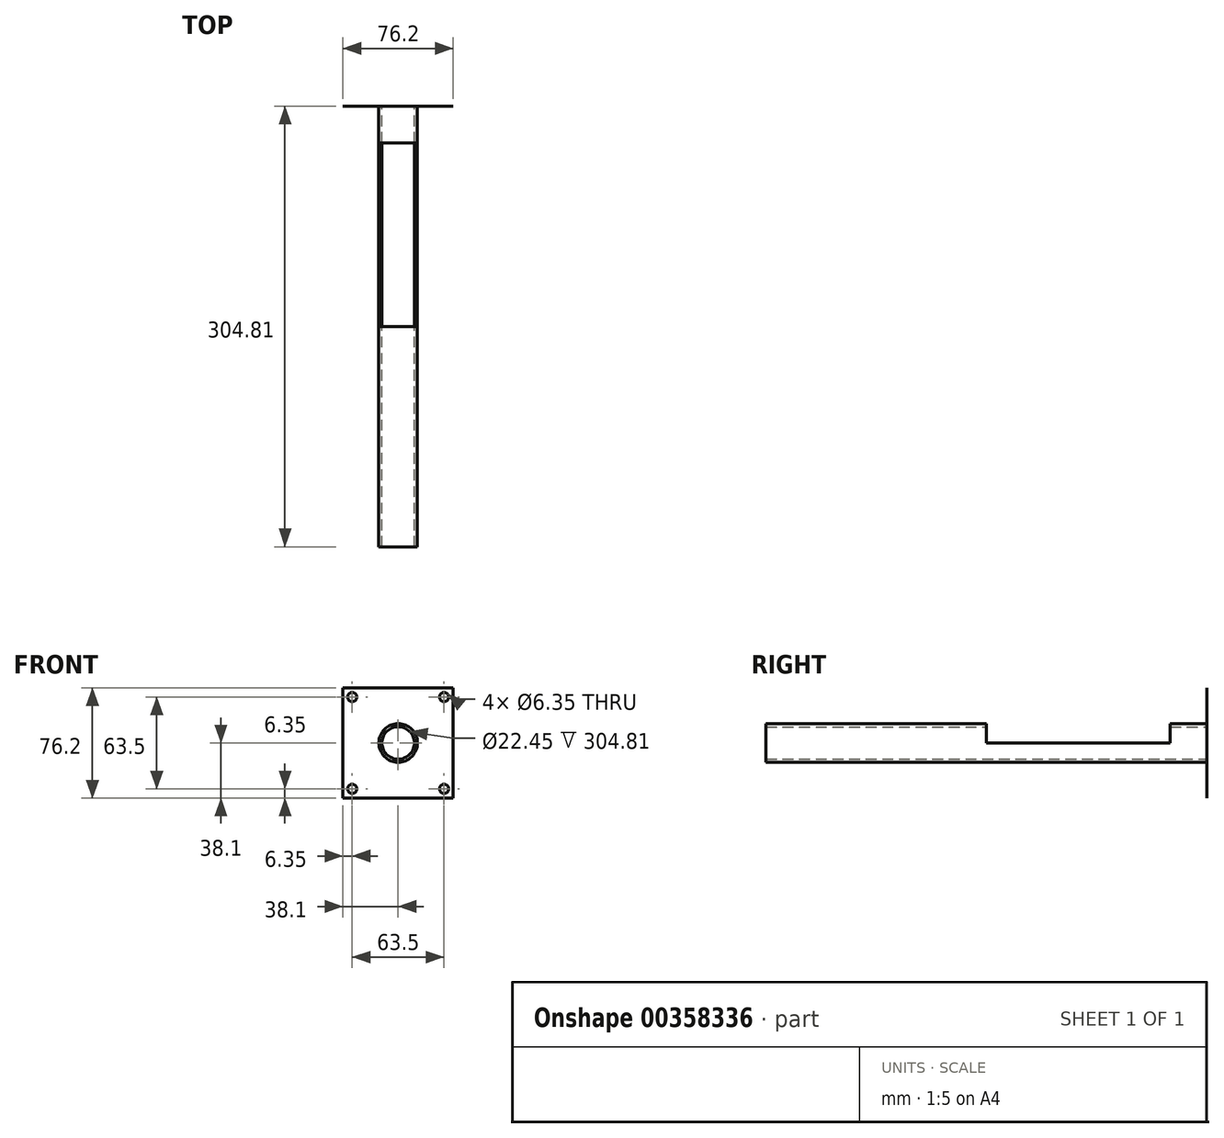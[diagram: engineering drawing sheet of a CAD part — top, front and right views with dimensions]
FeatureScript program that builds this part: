
annotation { "Feature Type Name" : "Feature", "Feature Type Description" : "" }
export const myFeature = defineFeature(function(context is Context, id is Id, definition is map)
    precondition{}
    {
        {
            var Q0;
            Q0=qCreatedBy(makeId("Front.planeOp"),FACE);
            var sketch = newSketch(context, id + "F0", { "sketchPlane" : qUnion([Q0])});
            skCircle(sketch, "E0", {"center": v(0, 0) * mm, "radius": 13.34 * mm});
            skCircle(sketch, "E1", {"center": v(0, 0) * mm, "radius": 11.23 * mm});
            skSolve(sketch);
        }
        {
            var Q0;
            Q0 = qSketchRegion(id + "F0", true);
            extrude(context, id + "F1", {"entities" : qUnion([Q0]), "offsetDistance" : 25 * mm, "depth" : 304.8 * mm});
        }
        {
            var Q0;
            Q0=makeQuery(id+"F1.opExtrude","CAP_FACE",FACE,{"disambiguationData":[OSD([sQuery(id+"F0.wireOp",EDGE,"E0"),sQuery(id+"F0.wireOp",EDGE,"E1")])],"isStart":true});
            var sketch = newSketch(context, id + "F2", { "sketchPlane" : qUnion([Q0])});
            skLineSegment(sketch, "E2.bottom", {"start": v(-38.1, 38.1) * mm, "end": v(38.1, 38.1) * mm});
            skLineSegment(sketch, "E2.top", {"start": v(-38.1, -38.1) * mm, "end": v(38.1, -38.1) * mm});
            skLineSegment(sketch, "E2.left", {"start": v(-38.1, 38.1) * mm, "end": v(-38.1, -38.1) * mm});
            skLineSegment(sketch, "E2.right", {"start": v(38.1, 38.1) * mm, "end": v(38.1, -38.1) * mm});
            skPoint(sketch, "E3", {"position": v(0, 38.1) * mm});
            skPoint(sketch, "E4", {"position": v(-38.1, 0) * mm});
            skCircle(sketch, "E5", {"center": v(0, 0) * mm, "radius": 11.23 * mm});
            skSolve(sketch);
        }
        {
            var Q0;
            Q0 = qSketchRegion(id + "F2", true);
            extrude(context, id + "F3", {"entities" : qUnion([Q0]), "operationType" : NewBodyOperationType.ADD, "depth" : 1 / 101.6 * mm});
        }
        {
            var Q0;
            Q0=qCreatedBy(makeId("Right.planeOp"),FACE);
            var sketch = newSketch(context, id + "F4", { "sketchPlane" : qUnion([Q0])});
            skLineSegment(sketch, "E6.bottom", {"start": v(-25.4, 30.23) * mm, "end": v(-152.4, 30.23) * mm});
            skLineSegment(sketch, "E6.top", {"start": v(-25.4, 0) * mm, "end": v(-152.4, 0) * mm});
            skLineSegment(sketch, "E6.left", {"start": v(-25.4, 30.23) * mm, "end": v(-25.4, 0) * mm});
            skLineSegment(sketch, "E6.right", {"start": v(-152.4, 30.23) * mm, "end": v(-152.4, 0) * mm});
            skSolve(sketch);
        }
        {
            var Q0;
            Q0 = qSketchRegion(id + "F4", true);
            extrude(context, id + "F5", {"entities" : qUnion([Q0]), "operationType" : NewBodyOperationType.REMOVE, "endBound" : BoundingType.THROUGH_ALL, "oppositeDirection" : true, "depth" : 25 * mm, "hasSecondDirection" : true, "secondDirectionBound" : BoundingType.THROUGH_ALL, "secondDirectionOppositeDirection" : false, "secondDirectionDepth" : 25 * mm});
        }
        {
            var Q0;
            Q0=makeQuery(id+"F5.boolean.opBoolean","MERGE",FACE,{"derivedFrom":[makeQuery(id+"F3.opExtrude","CAP_FACE",FACE,{"disambiguationData":[OSD([sQuery(id+"F2.wireOp",EDGE,"E2.bottom"),sQuery(id+"F2.wireOp",EDGE,"E2.top"),sQuery(id+"F2.wireOp",EDGE,"E2.left"),sQuery(id+"F2.wireOp",EDGE,"E2.right"),sQuery(id+"F2.wireOp",EDGE,"2QCN2HYW-vOLt-IU9v-KBP7-Mevz0STAQDgL")])],"isStart":true}),makeQuery(id+"F5.opExtrude","SWEPT_FACE",FACE,{"disambiguationData":[OSD([sQuery(id+"F4.wireOp",EDGE,"E6.left")])]})]});
            var sketch = newSketch(context, id + "F6", { "sketchPlane" : qUnion([Q0])});
            skCircle(sketch, "E7", {"center": v(-31.75, 31.75) * mm, "radius": 3.18 * mm});
            skCircle(sketch, "E8.0.1.0", {"center": v(-31.75, -31.75) * mm, "radius": 3.18 * mm});
            skCircle(sketch, "E8.1.0.0", {"center": v(31.75, 31.75) * mm, "radius": 3.18 * mm});
            skCircle(sketch, "E8.1.1.0", {"center": v(31.75, -31.75) * mm, "radius": 3.18 * mm});
            skLineSegment(sketch, "E8.direction1", {"start": v(-31.75, 31.75) * mm, "end": v(31.75, 31.75) * mm, "construction": true});
            skLineSegment(sketch, "E8.direction2", {"start": v(-31.75, 31.75) * mm, "end": v(-31.75, -31.75) * mm, "construction": true});
            skSolve(sketch);
        }
        {
            var Q0;
            Q0 = qSketchRegion(id + "F6", true);
            extrude(context, id + "F7", {"entities" : qUnion([Q0]), "operationType" : NewBodyOperationType.REMOVE, "endBound" : BoundingType.THROUGH_ALL, "oppositeDirection" : true, "depth" : 25 * mm});
        }
    });
